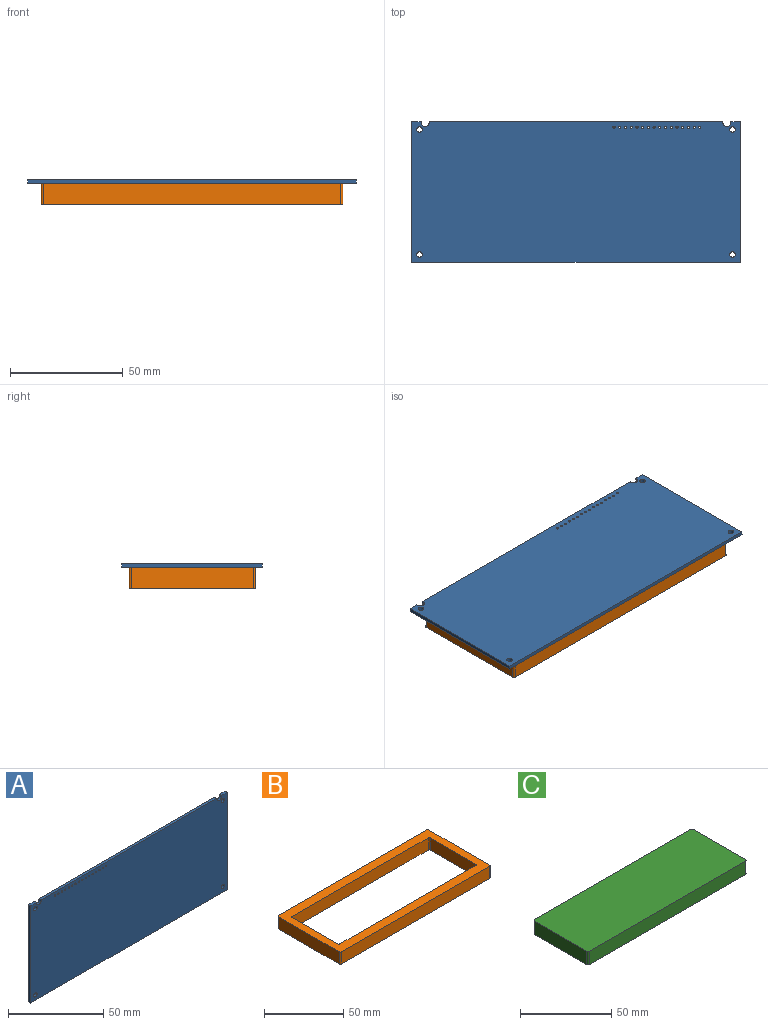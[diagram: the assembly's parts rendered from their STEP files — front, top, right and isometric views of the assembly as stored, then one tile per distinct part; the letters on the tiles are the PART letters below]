
ASSEMBLY  parts=3 mates=2
PART A: 34 faces, bbox 146x1.6x62.5 mm
  f0: plane 1.6x0.5mm, normal (1,0,0), area 0.8mm2, adj f1,f30,f32,f33
  f1: plane 130.5x1.6mm, normal (0,0,1), area 208.8mm2, adj f0,f2,f32,f33
  f2: plane 1.6x0.5mm, normal (-1,0,0), area 0.8mm2, adj f1,f3,f32,f33
  f3: cylinder r=1.75mm len=3.5mm, axis (0,1,0), area 8.8mm2, adj f2,f4,f32,f33
  f4: plane 1.6x0.5mm, normal (1,0,0), area 0.8mm2, adj f3,f5,f32,f33
  f5: plane 4.25x1.6mm, normal (0,0,1), area 6.8mm2, adj f4,f6,f32,f33
  f6: plane 62.5x1.6mm, normal (-1,0,0), area 100mm2, adj f5,f7,f32,f33
  f7: plane 146x1.6mm, normal (0,0,-1), area 233.6mm2, adj f6,f8,f32,f33
  f8: plane 62.5x1.6mm, normal (1,0,0), area 100mm2, adj f7,f9,f32,f33
  f9: plane 4.25x1.6mm, normal (0,0,1), area 6.8mm2, adj f8,f10,f32,f33
  f10: plane 1.6x0.5mm, normal (-1,0,0), area 0.8mm2, adj f9,f30,f32,f33
  f11: cylinder r=1.25mm len=2.5mm, axis (0,1,0), area 12.6mm2, adj f32,f33
  f12: cylinder r=1.25mm len=2.5mm, axis (0,1,0), area 12.6mm2, adj f32,f33
  f13: cylinder r=1.25mm len=2.5mm, axis (0,1,0), area 12.6mm2, adj f32,f33
  f14: cylinder r=0.5mm len=1.6mm, axis (0,1,0), area 5mm2, adj f32,f33
  f15: cylinder r=0.5mm len=1.6mm, axis (0,1,0), area 5mm2, adj f32,f33
  f16: cylinder r=0.5mm len=1.6mm, axis (0,1,0), area 5mm2, adj f32,f33
  f17: cylinder r=0.5mm len=1.6mm, axis (0,1,0), area 5mm2, adj f32,f33
  f18: cylinder r=0.5mm len=1.6mm, axis (0,1,0), area 5mm2, adj f32,f33
  f19: cylinder r=0.5mm len=1.6mm, axis (0,1,0), area 5mm2, adj f32,f33
  f20: cylinder r=0.5mm len=1.6mm, axis (0,1,0), area 5mm2, adj f32,f33
  f21: cylinder r=0.5mm len=1.6mm, axis (0,1,0), area 5mm2, adj f32,f33
  f22: cylinder r=0.5mm len=1.6mm, axis (0,1,0), area 5mm2, adj f32,f33
  f23: cylinder r=0.5mm len=1.6mm, axis (0,1,0), area 5mm2, adj f32,f33
  f24: cylinder r=0.5mm len=1.6mm, axis (0,1,0), area 5mm2, adj f32,f33
  f25: cylinder r=0.5mm len=1.6mm, axis (0,1,0), area 5mm2, adj f32,f33
  f26: cylinder r=0.5mm len=1.6mm, axis (0,1,0), area 5mm2, adj f32,f33
  f27: cylinder r=0.5mm len=1.6mm, axis (0,1,0), area 5mm2, adj f32,f33
  f28: cylinder r=0.5mm len=1.6mm, axis (0,1,0), area 5mm2, adj f32,f33
  f29: cylinder r=0.5mm len=1.6mm, axis (0,1,0), area 5mm2, adj f32,f33
  f30: cylinder r=1.75mm len=3.5mm, axis (0,1,0), area 8.8mm2, adj f0,f10,f32,f33
  f31: cylinder r=1.25mm len=2.5mm, axis (0,1,0), area 12.6mm2, adj f32,f33
  f32: plane 146x62.5mm, normal (0,-1,0), area 9079.7mm2, adj f0,f1,f2,f3,f4,f5,f6,f7
  f33: plane 146x62.5mm, normal (0,1,0), area 9079.7mm2, adj f0,f1,f2,f3,f4,f5,f6,f7
PART B: 18 faces, bbox 134x56.1x9.4 mm
  f0: plane 132x9.4mm, normal (0,1,0), area 1240.8mm2, adj f1,f15,f16,f17
  f1: cylinder r=1mm len=9.4mm, axis (0,0,-1), area 14.8mm2, adj f0,f2,f16,f17
  f2: plane 54.1x9.4mm, normal (-1,0,0), area 508.5mm2, adj f1,f3,f16,f17
  f3: cylinder r=1mm len=9.4mm, axis (0,0,-1), area 14.8mm2, adj f2,f4,f16,f17
  f4: plane 132x9.4mm, normal (0,-1,0), area 1240.8mm2, adj f3,f5,f16,f17
  f5: cylinder r=1mm len=9.4mm, axis (0,0,-1), area 14.8mm2, adj f4,f6,f16,f17
  f6: plane 54.1x9.4mm, normal (1,0,0), area 508.5mm2, adj f5,f15,f16,f17
  f7: cylinder r=1mm len=9.4mm, axis (0,0,-1), area 14.8mm2, adj f8,f14,f16,f17
  f8: plane 121x9.4mm, normal (0,-1,0), area 1137.4mm2, adj f7,f9,f16,f17
  f9: cylinder r=1mm len=9.4mm, axis (0,0,-1), area 14.8mm2, adj f8,f10,f16,f17
  f10: plane 40.5x9.4mm, normal (-1,0,0), area 380.7mm2, adj f9,f11,f16,f17
  f11: cylinder r=1mm len=9.4mm, axis (0,0,-1), area 14.8mm2, adj f10,f12,f16,f17
  f12: plane 121x9.4mm, normal (0,1,0), area 1137.4mm2, adj f11,f13,f16,f17
  f13: cylinder r=1mm len=9.4mm, axis (0,0,-1), area 14.8mm2, adj f12,f14,f16,f17
  f14: plane 40.5x9.4mm, normal (1,0,0), area 380.7mm2, adj f7,f13,f16,f17
  f15: cylinder r=1mm len=9.4mm, axis (0,0,-1), area 14.8mm2, adj f0,f6,f16,f17
  f16: plane 134x56.1mm, normal (0,0,1), area 2289.9mm2, adj f0,f1,f2,f3,f4,f5,f6,f7
  f17: plane 134x56.1mm, normal (0,0,-1), area 2289.9mm2, adj f0,f1,f2,f3,f4,f5,f6,f7
PART C: 10 faces, bbox 123x42.5x9 mm
  f0: plane 121x9mm, normal (0,1,0), area 1089mm2, adj f1,f7,f8,f9
  f1: cylinder r=1mm len=9mm, axis (0,0,-1), area 14.1mm2, adj f0,f2,f8,f9
  f2: plane 40.5x9mm, normal (-1,0,0), area 364.5mm2, adj f1,f3,f8,f9
  f3: cylinder r=1mm len=9mm, axis (0,0,-1), area 14.1mm2, adj f2,f4,f8,f9
  f4: plane 121x9mm, normal (0,-1,0), area 1089mm2, adj f3,f5,f8,f9
  f5: cylinder r=1mm len=9mm, axis (0,0,-1), area 14.1mm2, adj f4,f6,f8,f9
  f6: plane 40.5x9mm, normal (1,0,0), area 364.5mm2, adj f5,f7,f8,f9
  f7: cylinder r=1mm len=9mm, axis (0,0,-1), area 14.1mm2, adj f0,f6,f8,f9
  f8: plane 123x42.5mm, normal (0,0,1), area 5226.6mm2, adj f0,f1,f2,f3,f4,f5,f6,f7
  f9: plane 123x42.5mm, normal (0,0,-1), area 5226.6mm2, adj f0,f1,f2,f3,f4,f5,f6,f7
PLACE A rot(axis=(0,-0.71,-0.71),180deg) t=(-4.42,68.3,-15.24)mm
PLACE B rot(axis=(-0.06,0.21,0.98),0deg) t=(-4.47,68.22,-26.24)mm
PLACE C rot(axis=(0.29,-0.47,0.84),0deg) t=(-4.47,68.22,-25.84)mm
MATE fastened C.f8 <-> A.f32  axis (0,0,1) through (-4.47,68.22,-16.84)mm
MATE fastened B.f16 <-> A.f32  axis (0,0,1) through (-4.47,68.22,-16.84)mm
